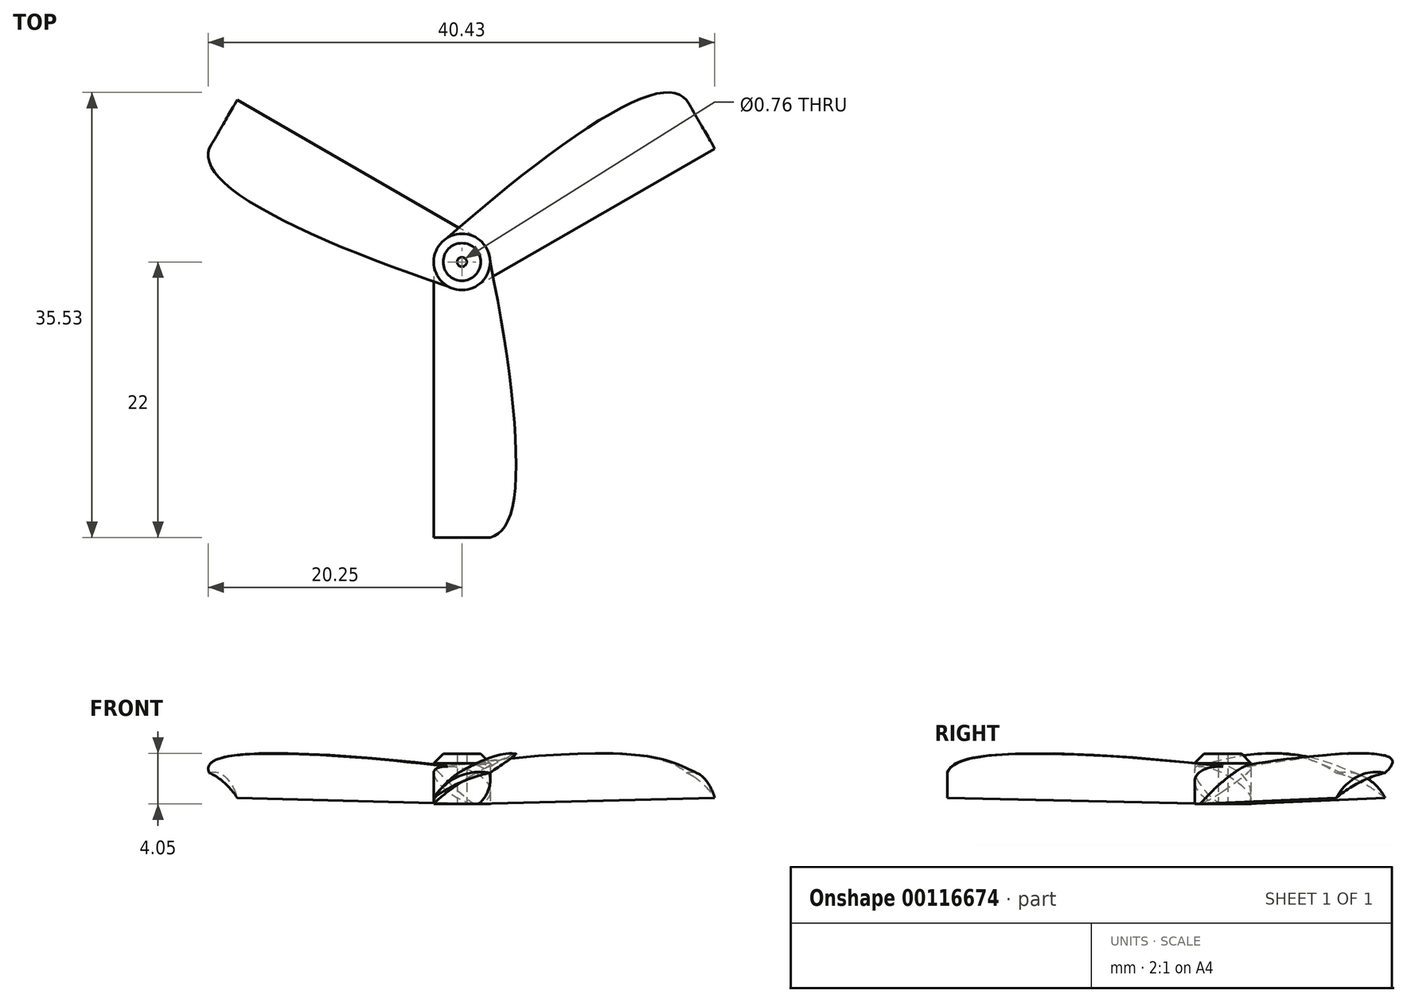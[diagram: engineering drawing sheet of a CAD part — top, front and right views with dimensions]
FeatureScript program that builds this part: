
annotation { "Feature Type Name" : "Feature", "Feature Type Description" : "" }
export const myFeature = defineFeature(function(context is Context, id is Id, definition is map)
    precondition{}
    {
        {
            var Q0;
            Q0=qCreatedBy(makeId("Top.planeOp"),FACE);
            var sketch = newSketch(context, id + "F0", { "sketchPlane" : qUnion([Q0])});
            skCircle(sketch, "E0", {"center": v(0, 0) * mm, "radius": 2.25 * mm});
            skSolve(sketch);
        }
        {
            var Q0;
            Q0 = qSketchRegion(id + "F0", true);
            extrude(context, id + "F1", {"entities" : qUnion([Q0]), "depth" : 4 * mm});
        }
        {
            var Q0;
            Q0=qCreatedBy(makeId("Front.planeOp"),FACE);
            var sketch = newSketch(context, id + "F2", { "sketchPlane" : qUnion([Q0])});
            skLineSegment(sketch, "E1", {"start": v(0, 0) * mm, "end": v(0, 3) * mm, "construction": true});
            skLineSegment(sketch, "E2.0", {"start": v(-2.25, 4) * mm, "end": v(2.25, 4) * mm, "construction": true});
            skLineSegment(sketch, "E3", {"start": v(0, 3) * mm, "end": v(2.25, 3) * mm, "construction": true});
            skLineSegment(sketch, "E4", {"start": v(0, 0) * mm, "end": v(-2.25, 0) * mm, "construction": true});
            skLineSegment(sketch, "E5", {"start": v(-2.25, 0) * mm, "end": v(2.25, 3) * mm, "construction": true});
            skLineSegment(sketch, "E6", {"start": v(0, 1.5) * mm, "end": v(-0.55, 2.33) * mm, "construction": true});
            skArc(sketch, "E7", {"start": v(2.25, 3) * mm, "mid": v(-0.55, 2.33) * mm, "end": v(-2.25, 0) * mm});
            skLineSegment(sketch, "E8", {"start": v(0, 1.5) * mm, "end": v(-0.14, 1.7) * mm, "construction": true});
            skArc(sketch, "E9", {"start": v(2.25, 3) * mm, "mid": v(-0.14, 1.7) * mm, "end": v(-2.25, 0) * mm});
            skSolve(sketch);
        }
        {
            var Q0;
            Q0=qCreatedBy(makeId("Front.planeOp"),FACE);
            cPlane(context, id + "F3", {"entities" : qUnion([Q0]), "cplaneType" : CPlaneType.OFFSET, "offset" : 22 * mm, "width" : 150 * mm, "height" : 150 * mm});
        }
        {
            var Q0;
            Q0=qCreatedBy(id+"F3.planeOp",FACE);
            var sketch = newSketch(context, id + "F4", { "sketchPlane" : qUnion([Q0])});
            skLineSegment(sketch, "E10.0", {"start": v(0, 3) * mm, "end": v(2.25, 3) * mm, "construction": true});
            skLineSegment(sketch, "E10.1", {"start": v(0, 0) * mm, "end": v(-2.25, 0) * mm, "construction": true});
            skLineSegment(sketch, "E11", {"start": v(-2.25, 0) * mm, "end": v(-2.25, 0.5) * mm, "construction": true});
            skLineSegment(sketch, "E12", {"start": v(2.25, 3) * mm, "end": v(2.25, 2.5) * mm, "construction": true});
            skLineSegment(sketch, "E13", {"start": v(-2.25, 0.5) * mm, "end": v(2.25, 2.5) * mm, "construction": true});
            skLineSegment(sketch, "E14", {"start": v(0, 1.5) * mm, "end": v(-0.3, 2.19) * mm, "construction": true});
            skLineSegment(sketch, "E15", {"start": v(0, 1.5) * mm, "end": v(-0.1, 1.73) * mm, "construction": true});
            skArc(sketch, "E16", {"start": v(2.25, 2.5) * mm, "mid": v(-0.3, 2.19) * mm, "end": v(-2.25, 0.5) * mm});
            skArc(sketch, "E17", {"start": v(2.25, 2.5) * mm, "mid": v(-0.1, 1.73) * mm, "end": v(-2.25, 0.5) * mm});
            skSolve(sketch);
        }
        {
            var Q0;
            Q0=sQuery(id+"F2.wireOp",EDGE,"E5");
            cPoint(context, id + "F5", {"entities" : qUnion([Q0]), "parameter" : 0.5});
        }
        {
            var Q0;
            Q0=sQuery(id+"F4.wireOp",VERTEX,"E16.start");
            var Q1;
            Q1 = qCreatedBy(id + "F5" ,VERTEX);
            var Q2;
            Q2=sQuery(id+"F2.wireOp",VERTEX,"E3.end");
            cPlane(context, id + "F6", {"entities" : qUnion([Q0, Q1, Q2]), "cplaneType" : CPlaneType.THREE_POINT, "offset" : 25 * mm, "width" : 150 * mm, "height" : 150 * mm});
        }
        {
            var Q0;
            Q0=qCreatedBy(id+"F6.planeOp",FACE);
            var sketch = newSketch(context, id + "F7", { "sketchPlane" : qUnion([Q0])});
            skPoint(sketch, "E18.0", {"position": v(3.54, 0.07) * mm});
            skPoint(sketch, "E18.1", {"position": v(3.54, -21.94) * mm});
            skLineSegment(sketch, "E19", {"start": v(3.54, 0.07) * mm, "end": v(3.54, -21.94) * mm, "construction": true});
            skLineSegment(sketch, "E20", {"start": v(3.54, 0.07) * mm, "end": v(3.54, -19.93) * mm, "construction": true});
            skLineSegment(sketch, "E21", {"start": v(3.54, -19.93) * mm, "end": v(5.54, -19.93) * mm, "construction": true});
            skFitSpline(sketch, "E22", {"points": [v(3.54, 0.07) * mm, v(5.54, -19.93) * mm, v(3.54, -21.94) * mm], "startDerivative": vector(8.9, -36.08) * mm, "endDerivative": vector(-9.07, -1.91) * mm});
            skSolve(sketch);
        }
        {
            var Q1;
            Q1 = qSketchRegion(id + "F2", true);
            var Q2;
            Q2 = qSketchRegion(id + "F4", true);
            var Q3;
            Q3=sQuery(id+"F7.wireOp",EDGE,"E22");
            loft(context, id + "F8", {"operationType" : NewBodyOperationType.ADD, "addGuides" : true, "sheetProfilesArray" : [{ "sheetProfileEntities" : qUnion([Q1]) }, { "sheetProfileEntities" : qUnion([Q2]) }], "guidesArray" : [{ "guideEntities" : qUnion([Q3]), "guideDerivativeType" : LoftGuideDerivativeType.DEFAULT, "guideDerivativeMagnitude" : 1 }]});
        }
        {
            var Q0;
            Q0=qCreatedBy(makeId("Front.planeOp"),FACE);
            var sketch = newSketch(context, id + "F9", { "sketchPlane" : qUnion([Q0])});
            skLineSegment(sketch, "E23", {"start": v(0, 0) * mm, "end": v(0, 5.95) * mm, "construction": true});
            skSolve(sketch);
        }
        {
            var Q0;
            Q0=makeQuery(id+"F1.opExtrude","SWEPT_BODY",BODY,{"disambiguationData":[OSD([sQuery(id+"F0.wireOp",EDGE,"E0")])]});
            var Q1;
            Q1=sQuery(id+"F9.wireOp",EDGE,"E23");
            circularPattern(context, id + "F10", {"operationType" : NewBodyOperationType.ADD, "entities" : qUnion([Q0]), "axis" : qUnion([Q1]), "angle" : 360 * degree, "instanceCount" : 3, "equalSpace" : true});
        }
        {
            var Q0;
            Q0=qCreatedBy(makeId("Top.planeOp"),FACE);
            var sketch = newSketch(context, id + "F11", { "sketchPlane" : qUnion([Q0])});
            skCircle(sketch, "E24", {"center": v(0, 0) * mm, "radius": 0.38 * mm});
            skSolve(sketch);
        }
        {
            var Q0;
            Q0 = qSketchRegion(id + "F11", true);
            extrude(context, id + "F12", {"entities" : qUnion([Q0]), "operationType" : NewBodyOperationType.REMOVE, "depth" : 25 * mm});
        }
        {
            var Q0;
            Q0=makeQuery(id+"F1.opExtrude","CAP_EDGE",EDGE,{"disambiguationData":[OSD([sQuery(id+"F0.wireOp",EDGE,"E0")])],"isStart":false});
            chamfer(context, id + "F13", {"entities" : qUnion([Q0]), "width" : .75 * mm, "tangentPropagation" : true});
        }
    });
